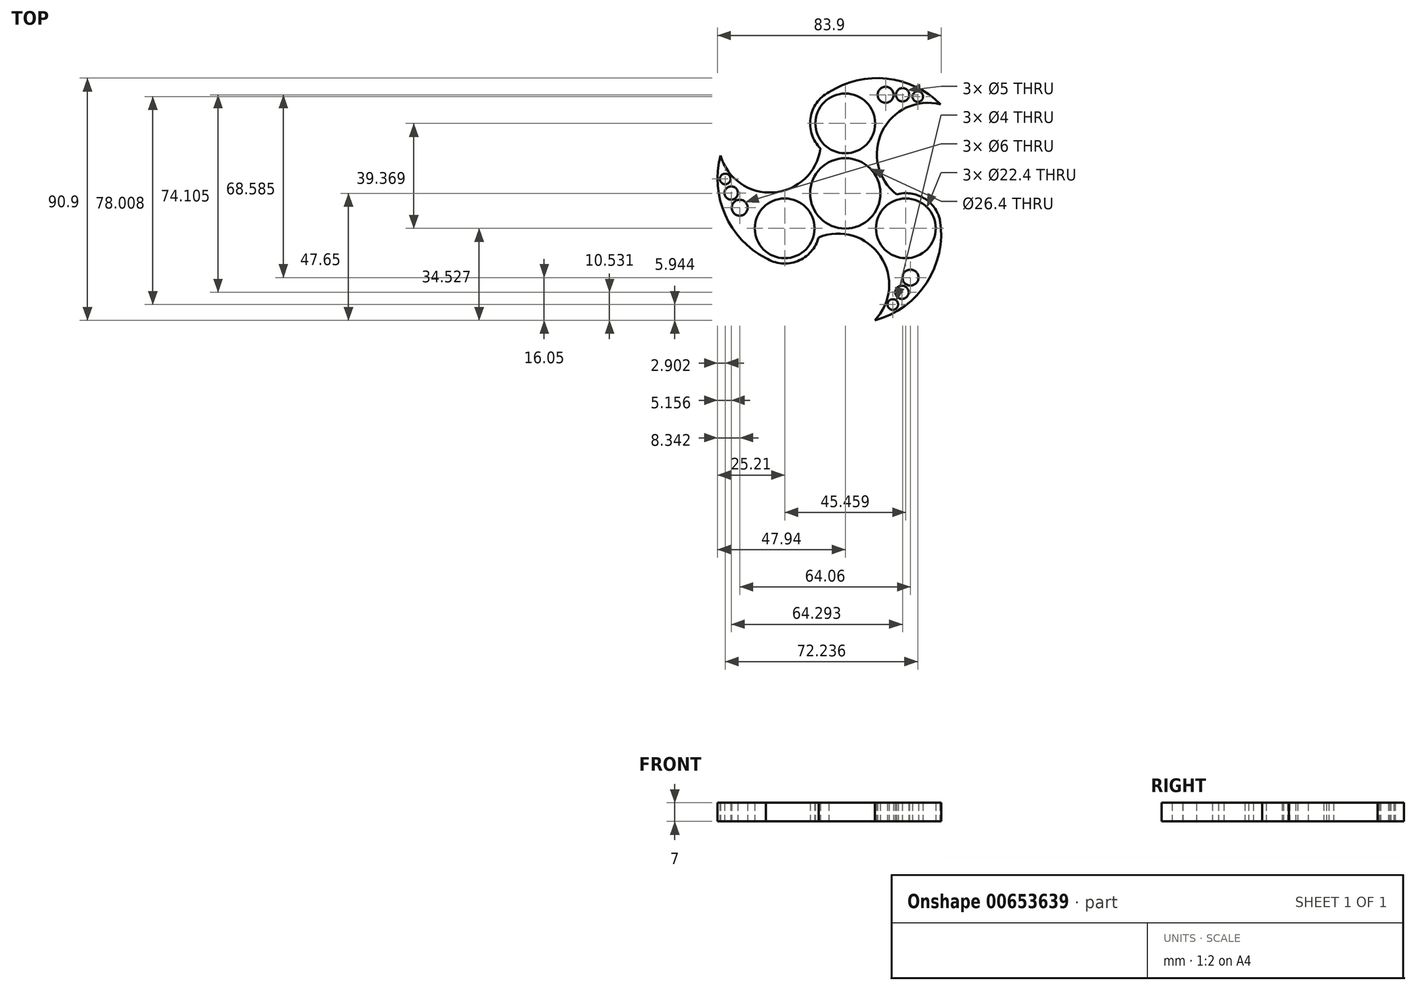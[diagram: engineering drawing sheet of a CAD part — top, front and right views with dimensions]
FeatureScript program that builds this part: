
annotation { "Feature Type Name" : "Feature", "Feature Type Description" : "" }
export const myFeature = defineFeature(function(context is Context, id is Id, definition is map)
    precondition{}
    {
        {
            var Q0;
            Q0=qCreatedBy(makeId("Top.planeOp"),FACE);
            var sketch = newSketch(context, id + "F0", { "sketchPlane" : qUnion([Q0])});
            skCircle(sketch, "E0", {"center": v(0, 0) * mm, "radius": 11.2 * mm});
            skCircle(sketch, "E1", {"center": v(0, 26.25) * mm, "radius": 11.2 * mm});
            skCircle(sketch, "E2", {"center": v(0, 26.25) * mm, "radius": 13.2 * mm});
            skCircle(sketch, "E3", {"center": v(0, 0) * mm, "radius": 13.2 * mm});
            skCircle(sketch, "E4.1.0", {"center": v(-22.73, -13.12) * mm, "radius": 13.2 * mm});
            skCircle(sketch, "E4.1.1", {"center": v(-22.73, -13.12) * mm, "radius": 11.2 * mm});
            skCircle(sketch, "E4.2.0", {"center": v(22.73, -13.12) * mm, "radius": 13.2 * mm});
            skCircle(sketch, "E4.2.1", {"center": v(22.73, -13.12) * mm, "radius": 11.2 * mm});
            skArc(sketch, "E5", {"start": v(35.73, 33.41) * mm, "mid": v(13.79, 23.2) * mm, "end": v(19.24, -0.4) * mm});
            skArc(sketch, "E6", {"start": v(35.73, 33.41) * mm, "mid": v(13.74, 43.2) * mm, "end": v(-9.14, 35.77) * mm});
            skArc(sketch, "E7.1.0", {"start": v(-46.8, 14.23) * mm, "mid": v(-44.28, -9.7) * mm, "end": v(-26.4, -25.8) * mm});
            skArc(sketch, "E7.1.1", {"start": v(-46.8, 14.23) * mm, "mid": v(-26.98, 0.34) * mm, "end": v(-9.28, 16.86) * mm});
            skArc(sketch, "E7.2.0", {"start": v(11.07, -47.65) * mm, "mid": v(30.54, -33.5) * mm, "end": v(35.55, -9.97) * mm});
            skArc(sketch, "E7.2.1", {"start": v(11.07, -47.65) * mm, "mid": v(13.2, -23.53) * mm, "end": v(-9.96, -16.47) * mm});
            skCircle(sketch, "E8", {"center": v(15.14, 36.99) * mm, "radius": 3 * mm});
            skCircle(sketch, "E9", {"center": v(21.5, 36.99) * mm, "radius": 2.5 * mm});
            skCircle(sketch, "E10", {"center": v(27.2, 36.3) * mm, "radius": 2 * mm});
            skCircle(sketch, "E11.1.0", {"center": v(-39.6, -5.38) * mm, "radius": 3 * mm});
            skCircle(sketch, "E11.1.1", {"center": v(-42.78, 0.13) * mm, "radius": 2.5 * mm});
            skCircle(sketch, "E11.1.2", {"center": v(-45.04, 5.4) * mm, "radius": 2 * mm});
            skCircle(sketch, "E11.2.0", {"center": v(24.46, -31.6) * mm, "radius": 3 * mm});
            skCircle(sketch, "E11.2.1", {"center": v(21.28, -37.12) * mm, "radius": 2.5 * mm});
            skCircle(sketch, "E11.2.2", {"center": v(17.84, -41.7) * mm, "radius": 2 * mm});
            skSolve(sketch);
        }
        {
            var Q0;
            {var subQ0=sQuery(id+"F0.wireOp",EDGE,"E6");var subQ1=sQuery(id+"F0.wireOp",EDGE,"E2");var subQ2=makeQuery(id+"F0.imprint","INTERSECT",VERTEX,{"disambiguationData":[OD(0.0)],"derivedFrom":[subQ1,subQ0]});Q0=makeQuery(id+"F0.imprint","IMPRINT",FACE,{"disambiguationData":[TD([[makeQuery(id+"F0.imprint","IMPRINT",EDGE,{"disambiguationData":[TD([[subQ2,1.0]])],"derivedFrom":subQ1}),1.0]])]});}
            var Q1;
            {var subQ0=sQuery(id+"F0.wireOp",EDGE,"E7.1.0");var subQ1=sQuery(id+"F0.wireOp",EDGE,"E4.1.0");var subQ2=makeQuery(id+"F0.imprint","INTERSECT",VERTEX,{"disambiguationData":[OD(0.0)],"derivedFrom":[subQ1,subQ0]});Q1=makeQuery(id+"F0.imprint","IMPRINT",FACE,{"disambiguationData":[TD([[makeQuery(id+"F0.imprint","IMPRINT",EDGE,{"disambiguationData":[TD([[subQ2,1.0]])],"derivedFrom":subQ1}),1.0]])]});}
            var Q2;
            {var subQ0=sQuery(id+"F0.wireOp",EDGE,"E7.2.0");var subQ1=sQuery(id+"F0.wireOp",EDGE,"E4.2.0");var subQ2=makeQuery(id+"F0.imprint","INTERSECT",VERTEX,{"disambiguationData":[OD(0.0)],"derivedFrom":[subQ1,subQ0]});Q2=makeQuery(id+"F0.imprint","IMPRINT",FACE,{"disambiguationData":[TD([[makeQuery(id+"F0.imprint","IMPRINT",EDGE,{"disambiguationData":[TD([[subQ2,1.0]])],"derivedFrom":subQ1}),1.0]])]});}
            var Q3;
            {var subQ0=sQuery(id+"F0.wireOp",EDGE,"E10");var subQ1=sQuery(id+"F0.wireOp",EDGE,"E5");var subQ2=makeQuery(id+"F0.imprint","INTERSECT",VERTEX,{"disambiguationData":[OD(0.0)],"derivedFrom":[subQ1,subQ0]});Q3=makeQuery(id+"F0.imprint","IMPRINT",FACE,{"disambiguationData":[TD([[makeQuery(id+"F0.imprint","IMPRINT",EDGE,{"disambiguationData":[TD([[subQ2,-1.0]])],"derivedFrom":subQ1}),1.0]])]});}
            var Q4;
            {var subQ0=sQuery(id+"F0.wireOp",EDGE,"E11.1.2");var subQ1=sQuery(id+"F0.wireOp",EDGE,"E7.1.1");var subQ2=makeQuery(id+"F0.imprint","INTERSECT",VERTEX,{"disambiguationData":[OD(0.0)],"derivedFrom":[subQ1,subQ0]});Q4=makeQuery(id+"F0.imprint","IMPRINT",FACE,{"disambiguationData":[TD([[makeQuery(id+"F0.imprint","IMPRINT",EDGE,{"disambiguationData":[TD([[subQ2,-1.0]])],"derivedFrom":subQ1}),1.0]])]});}
            var Q5;
            {var subQ0=sQuery(id+"F0.wireOp",EDGE,"E11.2.2");var subQ1=sQuery(id+"F0.wireOp",EDGE,"E7.2.1");var subQ2=makeQuery(id+"F0.imprint","INTERSECT",VERTEX,{"disambiguationData":[OD(0.0)],"derivedFrom":[subQ1,subQ0]});Q5=makeQuery(id+"F0.imprint","IMPRINT",FACE,{"disambiguationData":[TD([[makeQuery(id+"F0.imprint","IMPRINT",EDGE,{"disambiguationData":[TD([[subQ2,-1.0]])],"derivedFrom":subQ1}),1.0]])]});}
            var Q6;
            Q6=makeQuery(id+"F0.imprint","IMPRINT",FACE,{"disambiguationData":[TD([[makeQuery(id+"F0.imprint","IMPRINT",EDGE,{"derivedFrom":sQuery(id+"F0.wireOp",EDGE,"E1")}),-1.0]])]});
            var Q7;
            Q7=makeQuery(id+"F0.imprint","IMPRINT",FACE,{"disambiguationData":[TD([[makeQuery(id+"F0.imprint","IMPRINT",EDGE,{"derivedFrom":sQuery(id+"F0.wireOp",EDGE,"E4.1.1")}),-1.0]])]});
            var Q8;
            Q8=makeQuery(id+"F0.imprint","IMPRINT",FACE,{"disambiguationData":[TD([[makeQuery(id+"F0.imprint","IMPRINT",EDGE,{"derivedFrom":sQuery(id+"F0.wireOp",EDGE,"E4.2.1")}),-1.0]])]});
            var Q9;
            Q9=makeQuery(id+"F0.imprint","IMPRINT",FACE,{"disambiguationData":[TD([[makeQuery(id+"F0.imprint","IMPRINT",EDGE,{"derivedFrom":sQuery(id+"F0.wireOp",EDGE,"E11.1.0")}),-1.0]])]});
            var Q10;
            Q10=makeQuery(id+"F0.imprint","IMPRINT",FACE,{"disambiguationData":[TD([[makeQuery(id+"F0.imprint","IMPRINT",EDGE,{"derivedFrom":sQuery(id+"F0.wireOp",EDGE,"E8")}),-1.0]])]});
            var Q11;
            Q11=makeQuery(id+"F0.imprint","IMPRINT",FACE,{"disambiguationData":[TD([[makeQuery(id+"F0.imprint","IMPRINT",EDGE,{"derivedFrom":sQuery(id+"F0.wireOp",EDGE,"E11.2.0")}),-1.0]])]});
            extrude(context, id + "F1", {"entities" : qUnion([Q0, Q1, Q2, Q3, Q4, Q5, Q6, Q7, Q8, Q9, Q10, Q11]), "depth" : 7 * mm, "offsetDistance" : 25 * mm});
        }
    });
